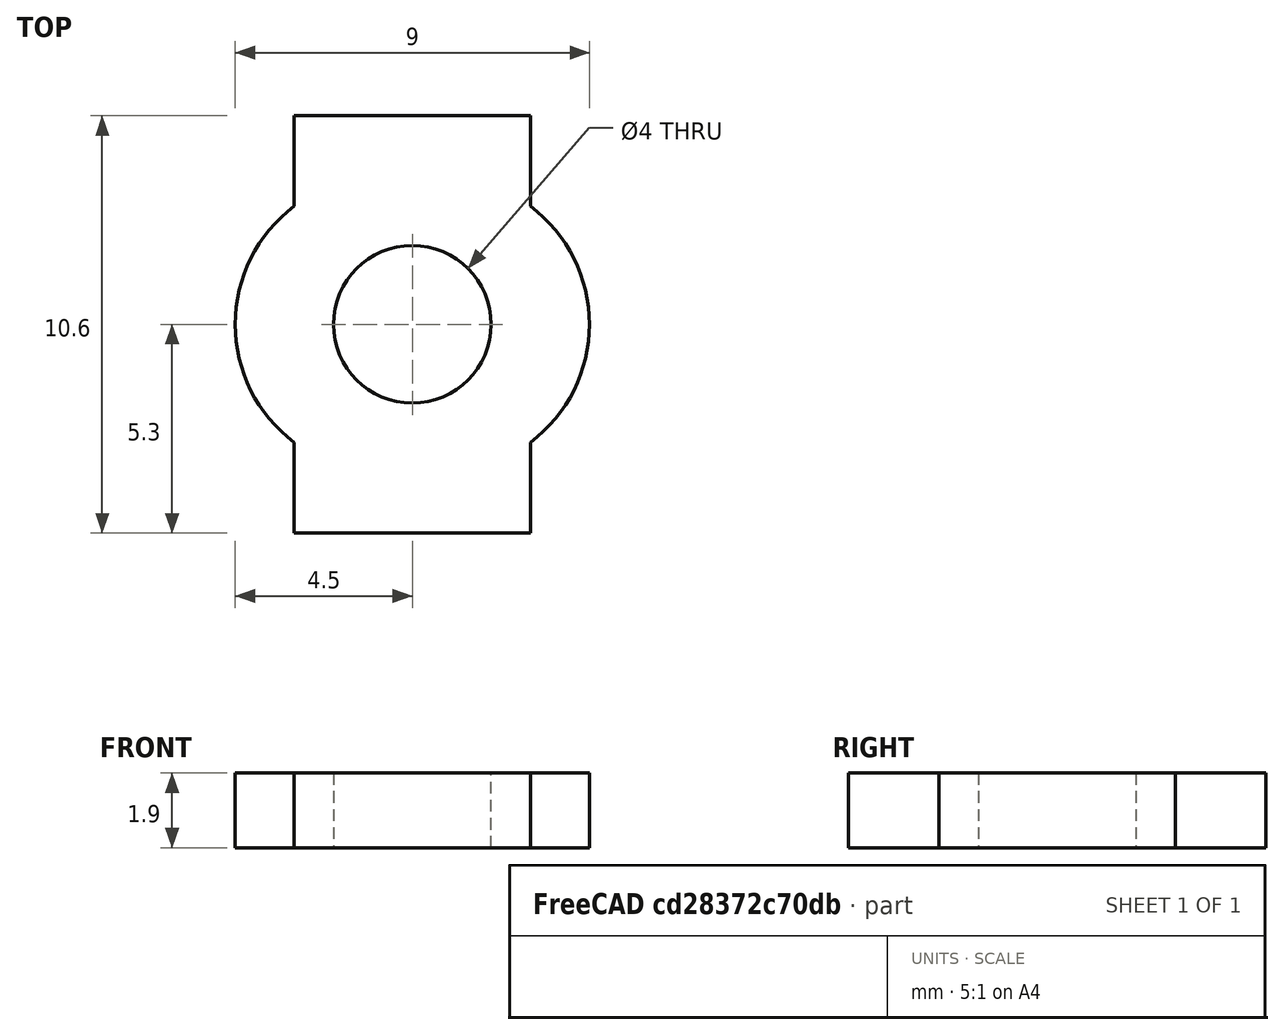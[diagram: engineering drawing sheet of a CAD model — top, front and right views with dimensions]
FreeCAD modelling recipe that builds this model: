
FCSTD DOCUMENT  (FreeCAD 0.20R29603 (Git))
Label: port
License: All rights reserved
LicenseURL: http://en.wikipedia.org/wiki/All_rights_reserved
objects: Sketcher::SketchObject×1, PartDesign::Pad×1, PartDesign::Body×1
note: 4 computed .brp shape members not serialized (recipe doc carries the construction recipe); baked Part::Feature solids carry a one-line shape summary decoded from their .brp

FEATURE [Sketcher::SketchObject] Sketch
  FullyConstrained = true
  MapMode = 5
  Support = -> [XY_Plane]
  sketch-geometry (18):
    g0: Circle CenterX=0 CenterY=0 CenterZ=0 NormalX=0 NormalY=0 NormalZ=1 AngleXU=0 Radius=2
    g1: LineSegment StartX=2 StartY=0 StartZ=0 EndX=4.5 EndY=0 EndZ=0
    g2: ArcOfCircle CenterX=0.75 CenterY=0 CenterZ=0 NormalX=0 NormalY=0 NormalZ=1 AngleXU=0 Radius=3.75 StartAngle=5.35589 EndAngle=7.21048
    g3: LineSegment StartX=3 StartY=-3 StartZ=0 EndX=3 EndY=3 EndZ=0
    g4: ArcOfCircle CenterX=-0.75 CenterY=0 CenterZ=0 NormalX=0 NormalY=0 NormalZ=1 AngleXU=0 Radius=3.75 StartAngle=2.2143 EndAngle=4.06889
    g5: LineSegment StartX=-2 StartY=0 StartZ=0 EndX=-4.5 EndY=0 EndZ=0
    g6: LineSegment StartX=-3 StartY=-3 StartZ=0 EndX=-3 EndY=3 EndZ=0
    g7: LineSegment StartX=0 StartY=0 StartZ=0 EndX=0 EndY=5.3 EndZ=0
    g8: LineSegment StartX=0 StartY=0 StartZ=0 EndX=0 EndY=-5.3 EndZ=0
    g9: LineSegment StartX=-3 StartY=-3 StartZ=0 EndX=-3 EndY=-5.3 EndZ=0
    g10: LineSegment StartX=3 StartY=-3 StartZ=0 EndX=3 EndY=-5.3 EndZ=0
    g11: LineSegment StartX=3 StartY=-5.3 StartZ=0 EndX=-3 EndY=-5.3 EndZ=0
    g12: LineSegment StartX=3 StartY=3 StartZ=0 EndX=3 EndY=5.3 EndZ=0
    g13: LineSegment StartX=-3 StartY=3 StartZ=0 EndX=-3 EndY=5.3 EndZ=0
    g14: LineSegment StartX=-3 StartY=5.3 StartZ=0 EndX=3 EndY=5.3 EndZ=0
    g15: LineSegment StartX=3 StartY=4.3 StartZ=0 EndX=0 EndY=4.3 EndZ=0
    g16: LineSegment StartX=0 StartY=4.3 StartZ=0 EndX=-3 EndY=4.3 EndZ=0
    g17: LineSegment StartX=0 StartY=4.3 StartZ=0 EndX=0 EndY=5.3 EndZ=0
  constraints (55):
    c: Coincident(g0,g-1)
    c: Diameter(g0) = 4
    c: PointOnObject(g1,g0)
    c: PointOnObject(g1,g-1)
    c: Perpendicular(g0,g1)
    c: DistanceX(g1,g1) = 2.5
    c: PointOnObject(g1,g2)
    c: Perpendicular(g2,g1)
    c: Coincident(g3,g2)
    c: Coincident(g3,g2)
    c: Vertical(g3)
    c: DistanceY(g3,g3) = 6
    c: PointOnObject(g4,g-1)
    c: PointOnObject(g5,g0)
    c: PointOnObject(g5,g4)
    c: Horizontal(g5)
    c: Perpendicular(g0,g5)
    c: Equal(g1,g5)
    c: Coincident(g6,g4)
    c: Coincident(g6,g4)
    c: Equal(g6,g3)
    c: Vertical(g6)
    c: Coincident(g7,g0)
    c: PointOnObject(g7,g-2)
    c: DistanceY(g7,g7) = 5.3
    c: Coincident(g8,g0)
    c: PointOnObject(g8,g-2)
    c: Equal(g8,g7)
    c: Coincident(g9,g4)
    c: Vertical(g9)
    c: Horizontal(g9,g8)
    c: Coincident(g10,g2)
    c: Vertical(g10)
    c: Horizontal(g10,g8)
    c: Coincident(g11,g10)
    c: Coincident(g11,g9)
    c: Coincident(g12,g2)
    c: Vertical(g12)
    c: Horizontal(g12,g7)
    c: Coincident(g13,g4)
    c: Vertical(g13)
    c: Horizontal(g13,g7)
    c: Coincident(g14,g13)
    c: Coincident(g14,g12)
    c: DistanceX(g14,g14) = 6
    c: PointOnObject(g15,g12)
    c: PointOnObject(g15,g7)
    c: Horizontal(g15)
    c: Coincident(g16,g15)
    c: PointOnObject(g16,g13)
    c: Horizontal(g16)
    c: Equal(g16,g15)
    c: Coincident(g17,g15)
    c: Coincident(g17,g7)
    c: DistanceY(g17,g17) = 1
FEATURE [PartDesign::Pad] Pad
  Direction = (0,0,1)
  Length = 1.9
  Length2 = 10
  Profile = -> Sketch
  ReferenceAxis = -> Sketch [N_Axis]
  Type = 0
FEATURE [PartDesign::Body] Body
  Group = -> [Sketch,Pad]
  Origin = -> Origin
  Tip = -> Pad
